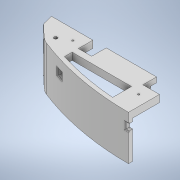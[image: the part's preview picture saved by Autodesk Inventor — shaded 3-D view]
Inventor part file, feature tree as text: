
AUTODESK INVENTOR PART (.ipt)
format: ipt  version: 2020 (Build 240168000, 168)  size: 543,232 bytes
history: native  units: mm
features: sketch x15, extrude x15, projected_geometry x8, other x6, hole x2, fillet x2
ambient origin geometry x8: Origin, YZ Plane, XZ Plane, XY Plane, X Axis, Y Axis, Z Axis, Center Point
bodies: Body1 (feature_tree)
feature tree (48):
  sketch  "스케치1"
  extrude  "돌출11"  Depth=657.5mm
  other  "작업 평면1"
  extrude  "돌출13"  Depth=585.0mm
  other  "작업 평면2"
  extrude  "돌출14"  Depth=0.872665mm
  other  "작업 평면3"
  extrude  "돌출15"  Depth=1299.898854mm
  other  "작업 평면4"
  extrude  "돌출16"  Depth=999.812583mm
  extrude  "돌출17"  Depth=2.356194mm
  extrude  "돌출18"  Depth=2.356194mm
  hole  "구멍3"  [1 undecoded]
  extrude  "돌출19"  Depth=2.356194mm
  hole  "구멍4"  [1 undecoded]
  extrude  "돌출20"  Depth=10.0mm
  extrude  "돌출21"  Depth=2.356194mm
  other  "작업 평면5"
  extrude  "돌출22"  Depth=2.356194mm
  other  "작업 평면6"
  extrude  "돌출23"  Depth=2.094395mm
  fillet  "모깎기4"  Radius=2.094395mm
  fillet  "모깎기5"  Radius=1.745329mm
  extrude  "돌출24"  Depth=1.745329mm
  extrude  "돌출25"  Depth=1.745329mm
  extrude  "돌출26"  Depth=18.0mm
  sketch  "스케치15"
  sketch  "스케치16"
  sketch  "스케치17"
  sketch  "스케치18"
  sketch  "스케치19"
  projected_geometry  "투영된 루프14"
  sketch  "스케치21"
  projected_geometry  "투영된 루프15"
  sketch  "스케치22"
  sketch  "스케치23"
  projected_geometry  "투영된 루프16"
  projected_geometry  "투영된 루프17"
  sketch  "스케치24"
  sketch  "스케치25"
  sketch  "스케치26"
  sketch  "스케치27"
  projected_geometry  "투영된 루프18"
  sketch  "스케치30"
  projected_geometry  "투영된 루프19"
  projected_geometry  "투영된 루프20"
  sketch  "스케치31"
  projected_geometry  "투영된 루프21"
note: 2 required parameter values undecoded (feature->parameter linkage not recoverable at this tier; creation-order binding heuristic only, values carry confidence <= 0.55)
